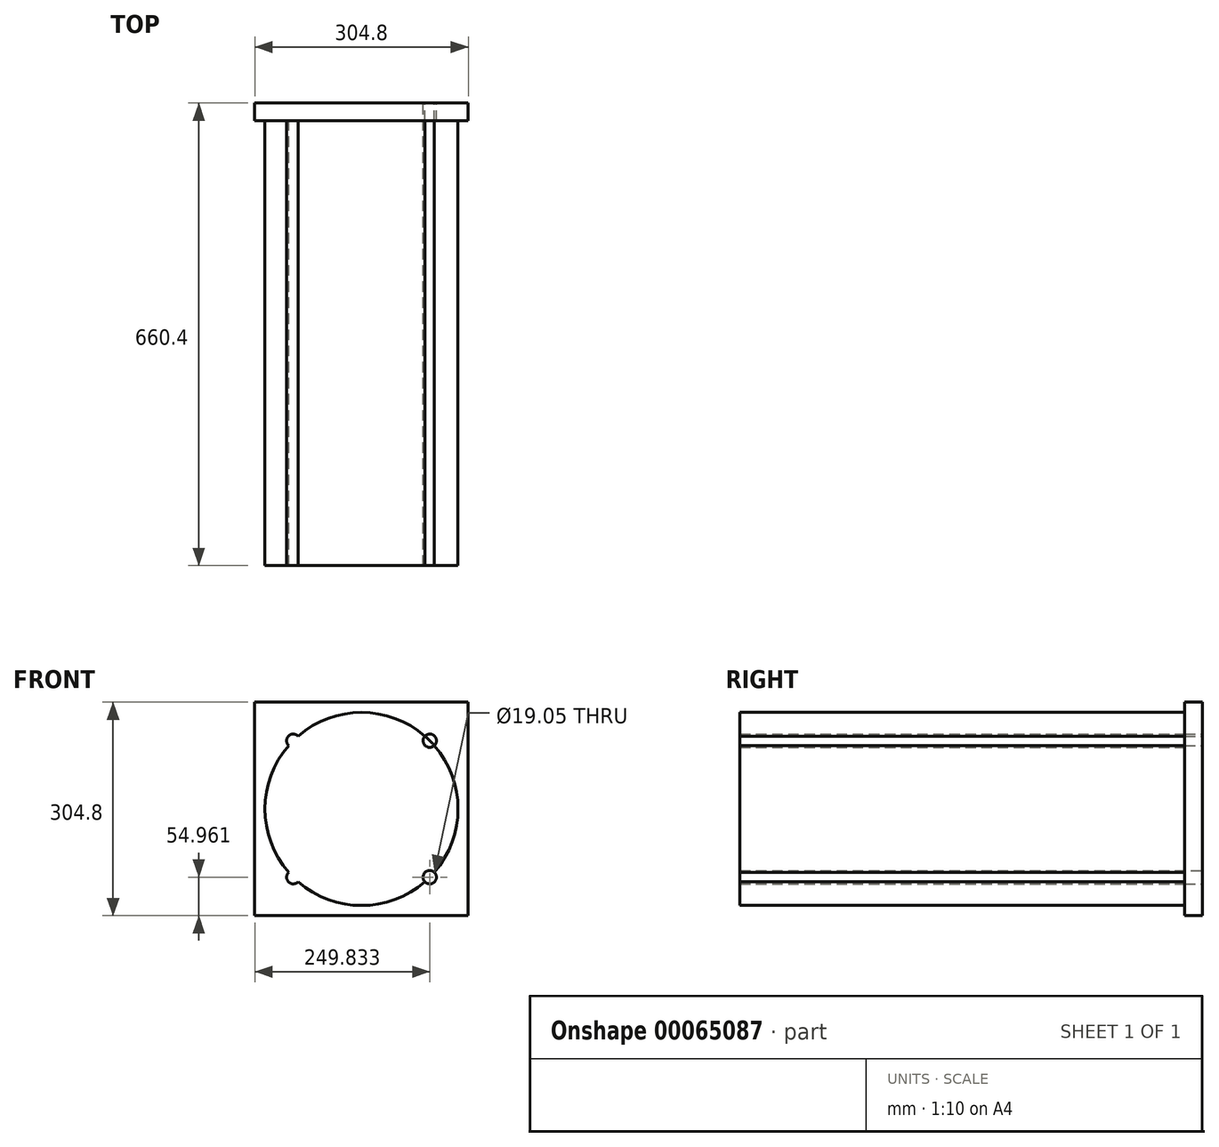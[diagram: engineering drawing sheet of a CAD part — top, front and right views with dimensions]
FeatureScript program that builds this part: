
annotation { "Feature Type Name" : "Feature", "Feature Type Description" : "" }
export const myFeature = defineFeature(function(context is Context, id is Id, definition is map)
    precondition{}
    {
        {
            var Q0;
            Q0=qCreatedBy(makeId("Front.planeOp"),FACE);
            var sketch = newSketch(context, id + "F0", { "sketchPlane" : qUnion([Q0])});
            skLineSegment(sketch, "E0.rect.bottom", {"start": v(140.94, 140.94) * mm, "end": v(-163.86, 140.94) * mm});
            skLineSegment(sketch, "E0.rect.top", {"start": v(140.94, -163.86) * mm, "end": v(-163.86, -163.86) * mm});
            skLineSegment(sketch, "E0.rect.left", {"start": v(140.94, 140.94) * mm, "end": v(140.94, -163.86) * mm});
            skLineSegment(sketch, "E0.rect.right", {"start": v(-163.86, 140.94) * mm, "end": v(-163.86, -163.86) * mm});
            skPoint(sketch, "E0.rect.middle", {"position": v(-11.46, -11.46) * mm});
            skCircle(sketch, "E1", {"center": v(-11.46, -11.46) * mm, "radius": 137.8 * mm});
            skCircle(sketch, "E2", {"center": v(-11.46, -11.46) * mm, "radius": 128.27 * mm, "construction": true});
            skLineSegment(sketch, "E3", {"start": v(-11.46, -11.46) * mm, "end": v(140.94, 140.94) * mm, "construction": true});
            skPoint(sketch, "E4", {"position": v(85.97, 85.97) * mm});
            skCircle(sketch, "E5", {"center": v(85.97, 85.97) * mm, "radius": 9.53 * mm});
            skLineSegment(sketch, "E6", {"start": v(-163.86, 140.94) * mm, "end": v(-11.46, -11.46) * mm, "construction": true});
            skCircle(sketch, "E7", {"center": v(-108.9, 85.97) * mm, "radius": 9.53 * mm});
            skLineSegment(sketch, "E8", {"start": v(-11.46, -11.46) * mm, "end": v(-163.86, -163.86) * mm, "construction": true});
            skLineSegment(sketch, "E9", {"start": v(-11.46, -11.46) * mm, "end": v(140.94, -163.86) * mm, "construction": true});
            skCircle(sketch, "E10", {"center": v(-108.9, -108.9) * mm, "radius": 9.53 * mm});
            skCircle(sketch, "E11", {"center": v(85.97, -108.9) * mm, "radius": 9.53 * mm});
            skSolve(sketch);
        }
        {
            var Q0;
            Q0 = qSketchRegion(id + "F0", true);
            var Q1;
            {var subQ0=sQuery(id+"F0.wireOp",EDGE,"E5");var subQ1=sQuery(id+"F0.wireOp",EDGE,"E1");var subQ11=makeQuery(id+"F0.imprint","INTERSECT",VERTEX,{"disambiguationData":[OD(0.0)],"derivedFrom":[subQ1,subQ0]});Q1=makeQuery(id+"F0.imprint","IMPRINT",FACE,{"disambiguationData":[TD([[makeQuery(id+"F0.imprint","IMPRINT",EDGE,{"disambiguationData":[TD([[subQ11,-1.0]])],"derivedFrom":subQ1}),1.0]])]});}
            extrude(context, id + "F1", {"entities" : qUnion([Q0, Q1]), "depth" : 25.4 * mm});
        }
        {
            var Q0;
            {var subQ0=sQuery(id+"F0.wireOp",EDGE,"E7");var subQ1=sQuery(id+"F0.wireOp",EDGE,"E1");var subQ2=makeQuery(id+"F0.imprint","INTERSECT",VERTEX,{"disambiguationData":[OD(0.0)],"derivedFrom":[subQ1,subQ0]});Q0=makeQuery(id+"F0.imprint","IMPRINT",FACE,{"disambiguationData":[TD([[makeQuery(id+"F0.imprint","IMPRINT",EDGE,{"disambiguationData":[TD([[subQ2,-1.0]])],"derivedFrom":subQ1}),-1.0]])]});}
            var Q1;
            {var subQ0=sQuery(id+"F0.wireOp",EDGE,"E7");var subQ1=sQuery(id+"F0.wireOp",EDGE,"E1");var subQ2=makeQuery(id+"F0.imprint","INTERSECT",VERTEX,{"disambiguationData":[OD(0.0)],"derivedFrom":[subQ1,subQ0]});Q1=makeQuery(id+"F0.imprint","IMPRINT",FACE,{"disambiguationData":[TD([[makeQuery(id+"F0.imprint","IMPRINT",EDGE,{"disambiguationData":[TD([[subQ2,-1.0]])],"derivedFrom":subQ1}),1.0]])]});}
            var Q2;
            {var subQ0=sQuery(id+"F0.wireOp",EDGE,"E5");var subQ1=sQuery(id+"F0.wireOp",EDGE,"E1");var subQ2=makeQuery(id+"F0.imprint","INTERSECT",VERTEX,{"disambiguationData":[OD(0.0)],"derivedFrom":[subQ1,subQ0]});Q2=makeQuery(id+"F0.imprint","IMPRINT",FACE,{"disambiguationData":[TD([[makeQuery(id+"F0.imprint","IMPRINT",EDGE,{"disambiguationData":[TD([[subQ2,1.0]])],"derivedFrom":subQ1}),1.0]])]});}
            var Q3;
            {var subQ0=sQuery(id+"F0.wireOp",EDGE,"E5");var subQ1=sQuery(id+"F0.wireOp",EDGE,"E1");var subQ2=makeQuery(id+"F0.imprint","INTERSECT",VERTEX,{"disambiguationData":[OD(0.0)],"derivedFrom":[subQ1,subQ0]});Q3=makeQuery(id+"F0.imprint","IMPRINT",FACE,{"disambiguationData":[TD([[makeQuery(id+"F0.imprint","IMPRINT",EDGE,{"disambiguationData":[TD([[subQ2,1.0]])],"derivedFrom":subQ1}),-1.0]])]});}
            var Q4;
            {var subQ0=sQuery(id+"F0.wireOp",EDGE,"E11");var subQ1=sQuery(id+"F0.wireOp",EDGE,"E1");var subQ2=makeQuery(id+"F0.imprint","INTERSECT",VERTEX,{"disambiguationData":[OD(0.0)],"derivedFrom":[subQ1,subQ0]});Q4=makeQuery(id+"F0.imprint","IMPRINT",FACE,{"disambiguationData":[TD([[makeQuery(id+"F0.imprint","IMPRINT",EDGE,{"disambiguationData":[TD([[subQ2,-1.0]])],"derivedFrom":subQ1}),1.0]])]});}
            var Q5;
            {var subQ0=sQuery(id+"F0.wireOp",EDGE,"E10");var subQ1=sQuery(id+"F0.wireOp",EDGE,"E1");var subQ2=makeQuery(id+"F0.imprint","INTERSECT",VERTEX,{"disambiguationData":[OD(0.0)],"derivedFrom":[subQ1,subQ0]});Q5=makeQuery(id+"F0.imprint","IMPRINT",FACE,{"disambiguationData":[TD([[makeQuery(id+"F0.imprint","IMPRINT",EDGE,{"disambiguationData":[TD([[subQ2,-1.0]])],"derivedFrom":subQ1}),-1.0]])]});}
            var Q6;
            {var subQ0=sQuery(id+"F0.wireOp",EDGE,"E10");var subQ1=sQuery(id+"F0.wireOp",EDGE,"E1");var subQ2=makeQuery(id+"F0.imprint","INTERSECT",VERTEX,{"disambiguationData":[OD(0.0)],"derivedFrom":[subQ1,subQ0]});Q6=makeQuery(id+"F0.imprint","IMPRINT",FACE,{"disambiguationData":[TD([[makeQuery(id+"F0.imprint","IMPRINT",EDGE,{"disambiguationData":[TD([[subQ2,-1.0]])],"derivedFrom":subQ1}),1.0]])]});}
            var Q7;
            {var subQ0=sQuery(id+"F0.wireOp",EDGE,"E11");var subQ1=sQuery(id+"F0.wireOp",EDGE,"E1");var subQ2=makeQuery(id+"F0.imprint","INTERSECT",VERTEX,{"disambiguationData":[OD(0.0)],"derivedFrom":[subQ1,subQ0]});Q7=makeQuery(id+"F0.imprint","IMPRINT",FACE,{"disambiguationData":[TD([[makeQuery(id+"F0.imprint","IMPRINT",EDGE,{"disambiguationData":[TD([[subQ2,-1.0]])],"derivedFrom":subQ1}),-1.0]])]});}
            extrude(context, id + "F2", {"entities" : qUnion([Q0, Q1, Q2, Q3, Q4, Q5, Q6, Q7]), "operationType" : NewBodyOperationType.ADD, "depth" : 660.4 * mm});
        }
    });
